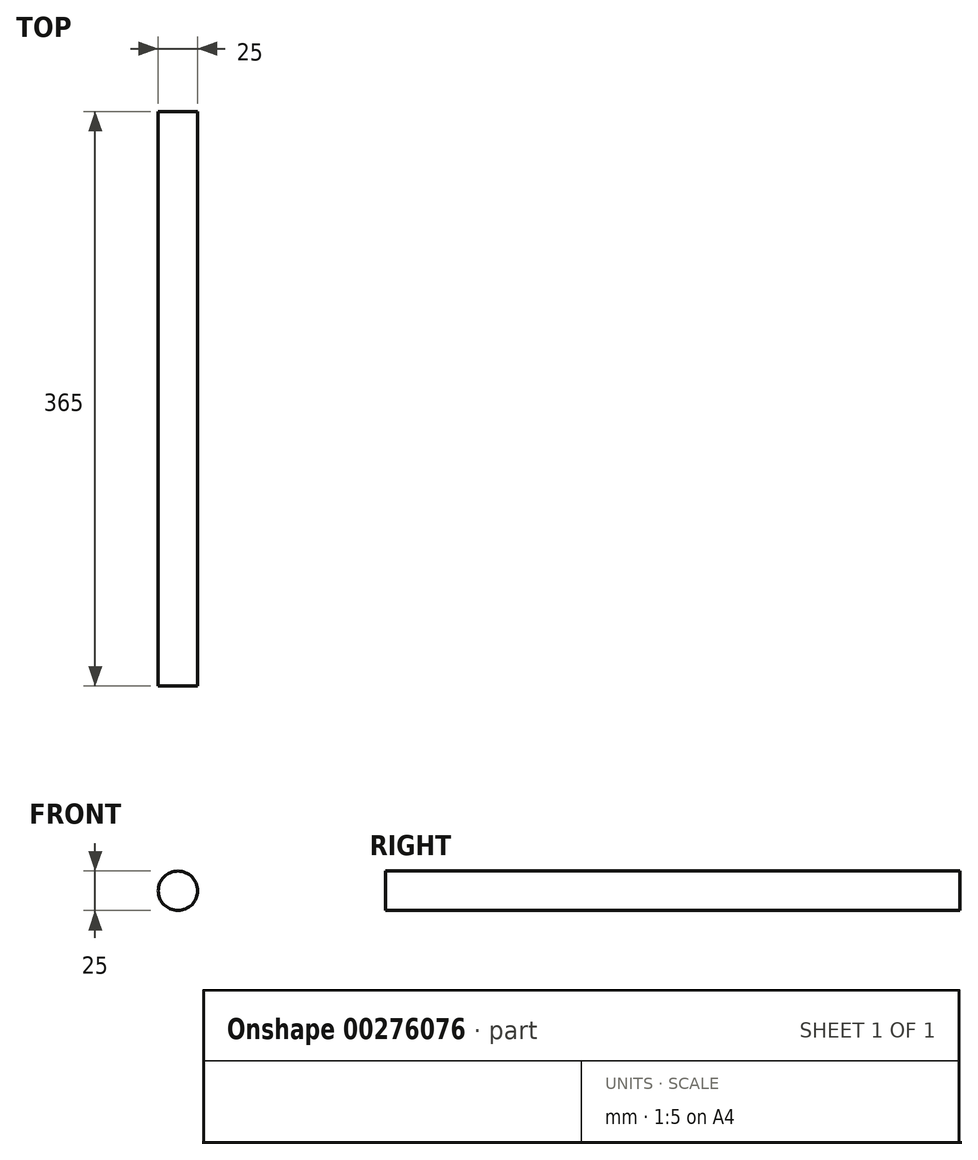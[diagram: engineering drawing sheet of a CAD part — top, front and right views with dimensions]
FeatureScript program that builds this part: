
annotation { "Feature Type Name" : "Feature", "Feature Type Description" : "" }
export const myFeature = defineFeature(function(context is Context, id is Id, definition is map)
    precondition{}
    {
        {
            var Q0;
            Q0=qCreatedBy(makeId("Front.planeOp"),FACE);
            var sketch = newSketch(context, id + "F0", { "sketchPlane" : qUnion([Q0])});
            skCircle(sketch, "E0", {"center": v(0, 0) * mm, "radius": 12.5 * mm});
            skSolve(sketch);
        }
        {
            var Q0;
            Q0=makeQuery(id+"F0.imprint","IMPRINT",FACE,{"disambiguationData":[TD([[makeQuery(id+"F0.imprint","IMPRINT",EDGE,{"derivedFrom":sQuery(id+"F0.wireOp",EDGE,"E0")}),1.0]])]});
            extrude(context, id + "F1", {"entities" : qUnion([Q0]), "endBound" : BoundingType.SYMMETRIC, "depth" : 365 * mm});
        }
    });
